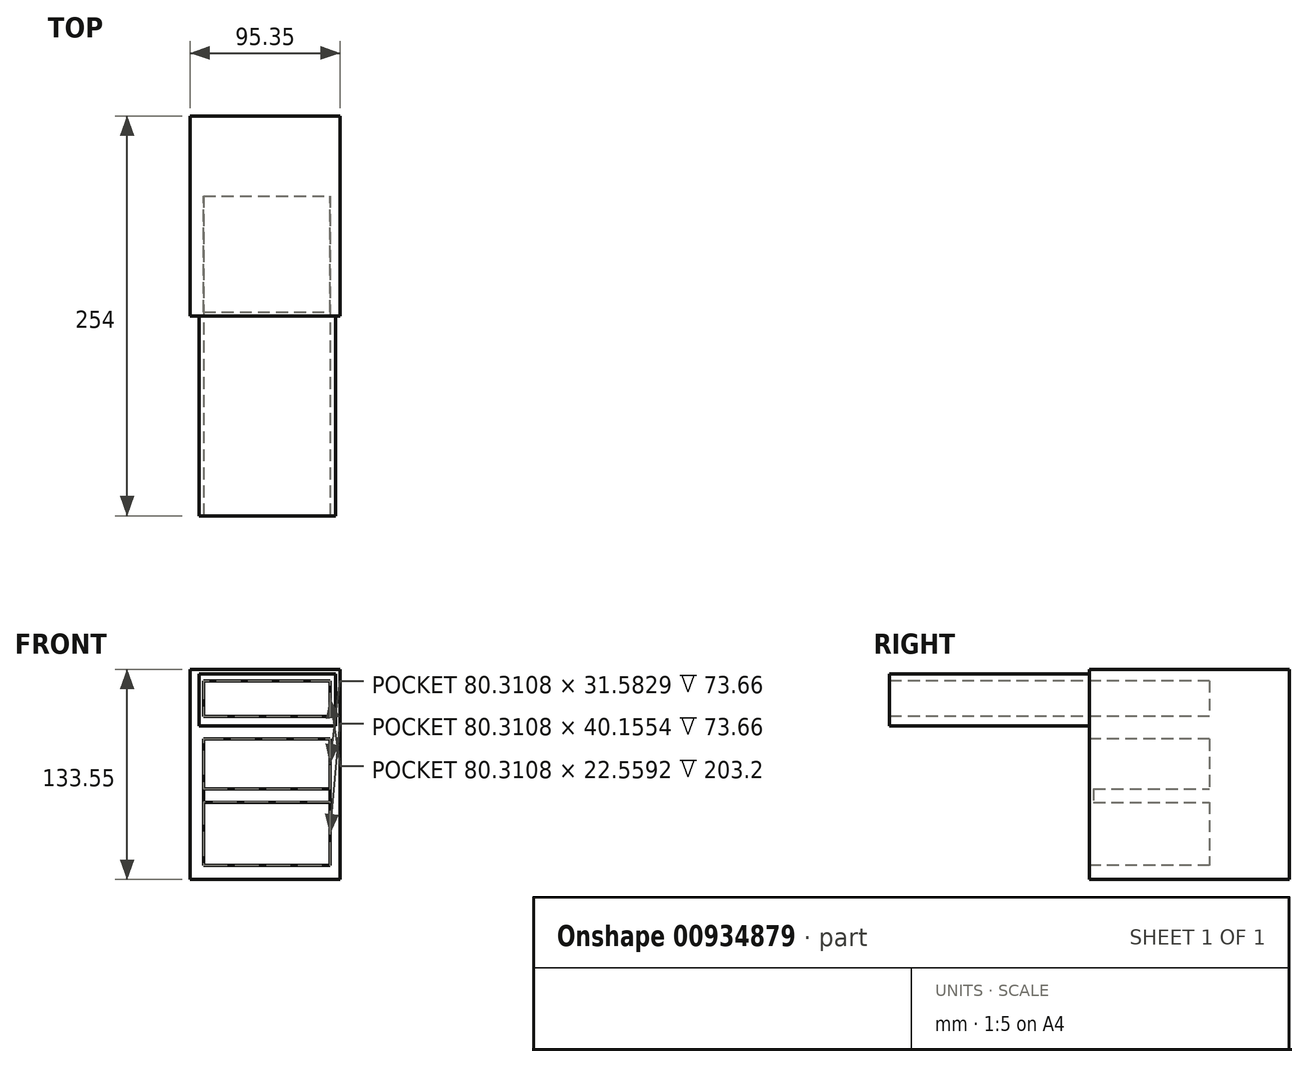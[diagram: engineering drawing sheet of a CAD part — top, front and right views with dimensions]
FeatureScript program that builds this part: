
annotation { "Feature Type Name" : "Feature", "Feature Type Description" : "" }
export const myFeature = defineFeature(function(context is Context, id is Id, definition is map)
    precondition{}
    {
        {
            var Q0;
            Q0=qCreatedBy(makeId("Front.planeOp"),FACE);
            var sketch = newSketch(context, id + "F0", { "sketchPlane" : qUnion([Q0])});
            skLineSegment(sketch, "E0.bottom", {"start": v(-50.98, 66.93) * mm, "end": v(44.37, 66.93) * mm});
            skLineSegment(sketch, "E0.top", {"start": v(-50.98, -66.62) * mm, "end": v(44.37, -66.62) * mm});
            skLineSegment(sketch, "E0.left", {"start": v(-50.98, 66.93) * mm, "end": v(-50.98, -66.62) * mm});
            skLineSegment(sketch, "E0.right", {"start": v(44.37, 66.93) * mm, "end": v(44.37, -66.62) * mm});
            skSolve(sketch);
        }
        {
            var Q0;
            Q0 = qSketchRegion(id + "F0", true);
            extrude(context, id + "F1", {"entities" : qUnion([Q0]), "depth" : 127 * mm, "offsetDistance" : 25.4 * mm});
        }
        {
            var Q0;
            Q0=makeQuery(id+"F1.opExtrude","CAP_FACE",FACE,{"disambiguationData":[OSD([sQuery(id+"F0.wireOp",EDGE,"E0.bottom"),sQuery(id+"F0.wireOp",EDGE,"E0.top"),sQuery(id+"F0.wireOp",EDGE,"E0.left"),sQuery(id+"F0.wireOp",EDGE,"E0.right")])],"isStart":false});
            var sketch = newSketch(context, id + "F2", { "sketchPlane" : qUnion([Q0])});
            skLineSegment(sketch, "E1.bottom", {"start": v(-42.26, 59.7) * mm, "end": v(38.05, 59.7) * mm});
            skLineSegment(sketch, "E1.top", {"start": v(-42.26, 37.15) * mm, "end": v(38.05, 37.15) * mm});
            skLineSegment(sketch, "E1.left", {"start": v(-42.26, 59.7) * mm, "end": v(-42.26, 37.15) * mm});
            skLineSegment(sketch, "E1.right", {"start": v(38.05, 59.7) * mm, "end": v(38.05, 37.15) * mm});
            skLineSegment(sketch, "E2.bottom", {"start": v(-42.26, 22.7) * mm, "end": v(38.05, 22.7) * mm});
            skLineSegment(sketch, "E2.top", {"start": v(-42.26, -57.6) * mm, "end": v(38.05, -57.6) * mm});
            skLineSegment(sketch, "E2.left", {"start": v(-42.26, 22.7) * mm, "end": v(-42.26, -57.6) * mm});
            skLineSegment(sketch, "E2.right", {"start": v(38.05, 22.7) * mm, "end": v(38.05, -57.6) * mm});
            skSolve(sketch);
        }
        {
            var Q0;
            Q0=makeQuery(id+"F2.imprint","IMPRINT",FACE,{"disambiguationData":[TD([[makeQuery(id+"F2.imprint","IMPRINT",EDGE,{"derivedFrom":sQuery(id+"F2.wireOp",EDGE,"E1.bottom")}),-1.0]])]});
            var Q1;
            Q1=makeQuery(id+"F2.imprint","IMPRINT",FACE,{"disambiguationData":[TD([[makeQuery(id+"F2.imprint","IMPRINT",EDGE,{"derivedFrom":sQuery(id+"F2.wireOp",EDGE,"E2.bottom")}),-1.0]])]});
            extrude(context, id + "F3", {"entities" : qUnion([Q0, Q1]), "operationType" : NewBodyOperationType.REMOVE, "oppositeDirection" : true, "depth" : 76.2 * mm, "offsetDistance" : 25.4 * mm});
        }
        {
            var Q0;
            Q0=makeQuery(id+"F3.boolean.opBoolean","COPY",FACE,{"derivedFrom":makeQuery(id+"F3.opExtrude","CAP_FACE",FACE,{"disambiguationData":[OSD([sQuery(id+"F2.wireOp",EDGE,"E2.bottom"),sQuery(id+"F2.wireOp",EDGE,"E2.top"),sQuery(id+"F2.wireOp",EDGE,"E2.left"),sQuery(id+"F2.wireOp",EDGE,"E2.right")])],"isStart":false})});
            var sketch = newSketch(context, id + "F4", { "sketchPlane" : qUnion([Q0])});
            skLineSegment(sketch, "E3.bottom", {"start": v(-42.26, -8.87) * mm, "end": v(38.05, -8.87) * mm});
            skLineSegment(sketch, "E3.top", {"start": v(-42.26, -17.45) * mm, "end": v(38.05, -17.45) * mm});
            skLineSegment(sketch, "E3.left", {"start": v(-42.26, -8.87) * mm, "end": v(-42.26, -17.45) * mm});
            skLineSegment(sketch, "E3.right", {"start": v(38.05, -8.87) * mm, "end": v(38.05, -17.45) * mm});
            skSolve(sketch);
        }
        {
            var Q0;
            Q0=makeQuery(id+"F4.imprint","IMPRINT",FACE,{"disambiguationData":[TD([[makeQuery(id+"F4.imprint","IMPRINT",EDGE,{"derivedFrom":sQuery(id+"F4.wireOp",EDGE,"E3.bottom")}),-1.0]])]});
            extrude(context, id + "F5", {"entities" : qUnion([Q0]), "operationType" : NewBodyOperationType.ADD, "depth" : 73.66 * mm, "offsetDistance" : 25.4 * mm});
        }
        {
            var Q0;
            Q0=makeQuery(id+"F1.opExtrude","CAP_FACE",FACE,{"disambiguationData":[OSD([sQuery(id+"F0.wireOp",EDGE,"E0.bottom"),sQuery(id+"F0.wireOp",EDGE,"E0.top"),sQuery(id+"F0.wireOp",EDGE,"E0.left"),sQuery(id+"F0.wireOp",EDGE,"E0.right")])],"isStart":false});
            var sketch = newSketch(context, id + "F6", { "sketchPlane" : qUnion([Q0])});
            skLineSegment(sketch, "E4.bottom", {"start": v(-45.27, 63.92) * mm, "end": v(41.66, 63.92) * mm});
            skLineSegment(sketch, "E4.top", {"start": v(-45.27, 31.13) * mm, "end": v(41.66, 31.13) * mm});
            skLineSegment(sketch, "E4.left", {"start": v(-45.27, 63.92) * mm, "end": v(-45.27, 31.13) * mm});
            skLineSegment(sketch, "E4.right", {"start": v(41.66, 63.92) * mm, "end": v(41.66, 31.13) * mm});
            skSolve(sketch);
        }
        {
            var Q0;
            Q0=makeQuery(id+"F6.imprint","IMPRINT",FACE,{"disambiguationData":[TD([[makeQuery(id+"F6.imprint","IMPRINT",EDGE,{"derivedFrom":sQuery(id+"F6.wireOp",EDGE,"E4.bottom")}),-1.0]])]});
            extrude(context, id + "F7", {"entities" : qUnion([Q0]), "operationType" : NewBodyOperationType.ADD, "depth" : 127 * mm, "offsetDistance" : 25.4 * mm});
        }
    });
